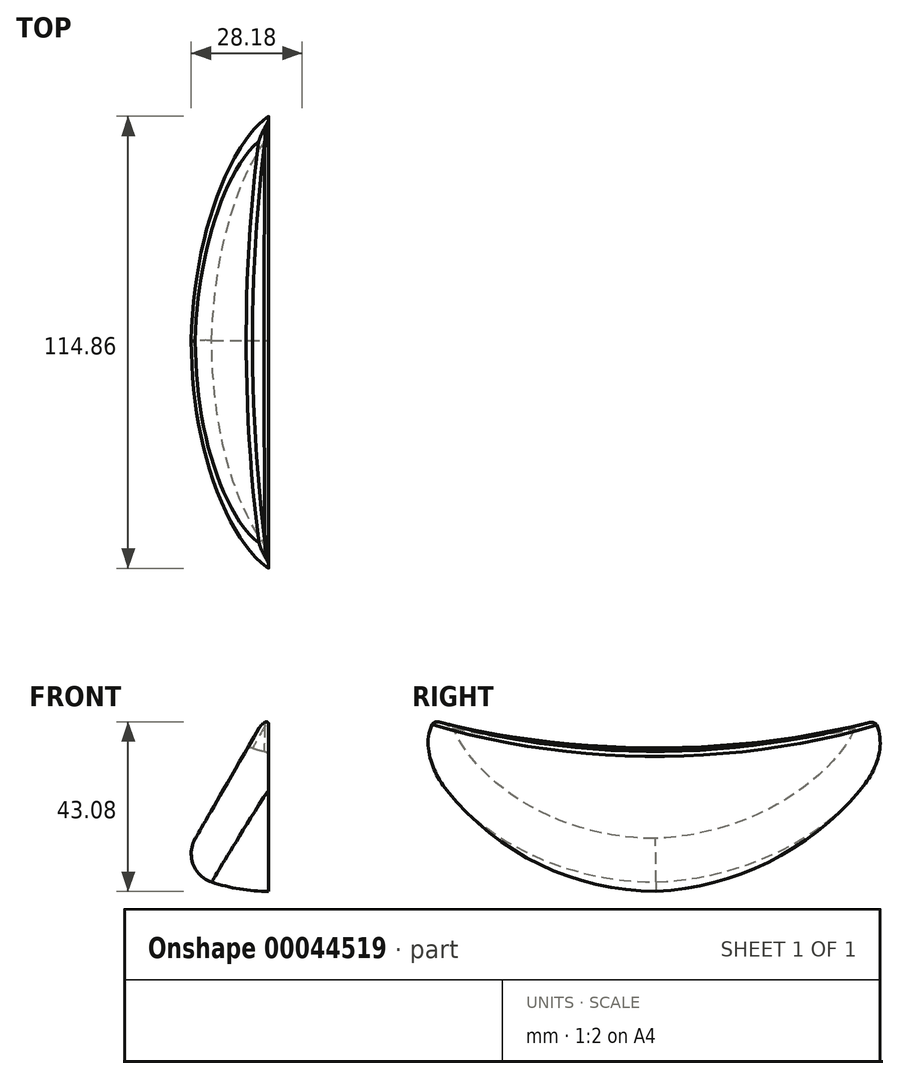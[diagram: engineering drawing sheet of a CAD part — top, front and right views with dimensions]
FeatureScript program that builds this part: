
annotation { "Feature Type Name" : "Feature", "Feature Type Description" : "" }
export const myFeature = defineFeature(function(context is Context, id is Id, definition is map)
    precondition{}
    {
        {
            var Q0;
            Q0=qCreatedBy(makeId("Right.planeOp"),FACE);
            var sketch = newSketch(context, id + "F0", { "sketchPlane" : qUnion([Q0])});
            skLineSegment(sketch, "E0", {"start": v(0, 0) * mm, "end": v(63.82, 0) * mm});
            skArc(sketch, "E1", {"start": v(0, -45.7) * mm, "mid": v(38.63, -32.23) * mm, "end": v(63.82, 0) * mm});
            skArc(sketch, "E2", {"start": v(-64.2, 0) * mm, "mid": v(-39.37, -33.06) * mm, "end": v(0, -45.7) * mm});
            skArc(sketch, "E3", {"start": v(-64.2, 0) * mm, "mid": v(-0.2, -10.22) * mm, "end": v(63.82, 0) * mm});
            skSolve(sketch);
        }
        {
            var Q0;
            Q0=makeQuery(id+"F0.imprint","IMPRINT",FACE,{"disambiguationData":[TD([[makeQuery(id+"F0.imprint","IMPRINT",EDGE,{"derivedFrom":sQuery(id+"F0.wireOp",EDGE,"E1")}),1.0]])]});
            var Q1;
            Q1=sQuery(id+"F0.wireOp",EDGE,"E0");
            revolve(context, id + "F1", {"entities" : qUnion([Q0]), "axis" : qUnion([Q1]), "revolveType" : RevolveType.ONE_DIRECTION, "angle" : 30 * degree});
        }
        {
            var Q0;
            Q0=makeQuery(id+"F1.opRevolve","CAP_EDGE",EDGE,{"disambiguationData":[OSD([sQuery(id+"F0.wireOp",EDGE,"E3")])],"isStart":true});
            var Q1;
            Q1=makeQuery(id+"F1.opRevolve","CAP_EDGE",EDGE,{"disambiguationData":[OSD([sQuery(id+"F0.wireOp",EDGE,"E3")])],"isStart":false});
            fillet(context, id + "F2", {"entities" : qUnion([Q0, Q1]), "radius" : 1.27 * mm, "tangentPropagation" : true, "allowEdgeOverflow" : false});
        }
        {
            var Q0;
            Q0=makeQuery(id+"F1.opRevolve","CAP_EDGE",EDGE,{"disambiguationData":[OSD([sQuery(id+"F0.wireOp",EDGE,"E2")])],"isStart":false});
            var Q1;
            Q1=makeQuery(id+"F1.opRevolve","CAP_EDGE",EDGE,{"disambiguationData":[OSD([sQuery(id+"F0.wireOp",EDGE,"E1")])],"isStart":false});
            fillet(context, id + "F3", {"entities" : qUnion([Q0, Q1]), "radius" : 7.62 * mm, "tangentPropagation" : true, "allowEdgeOverflow" : false});
        }
    });
